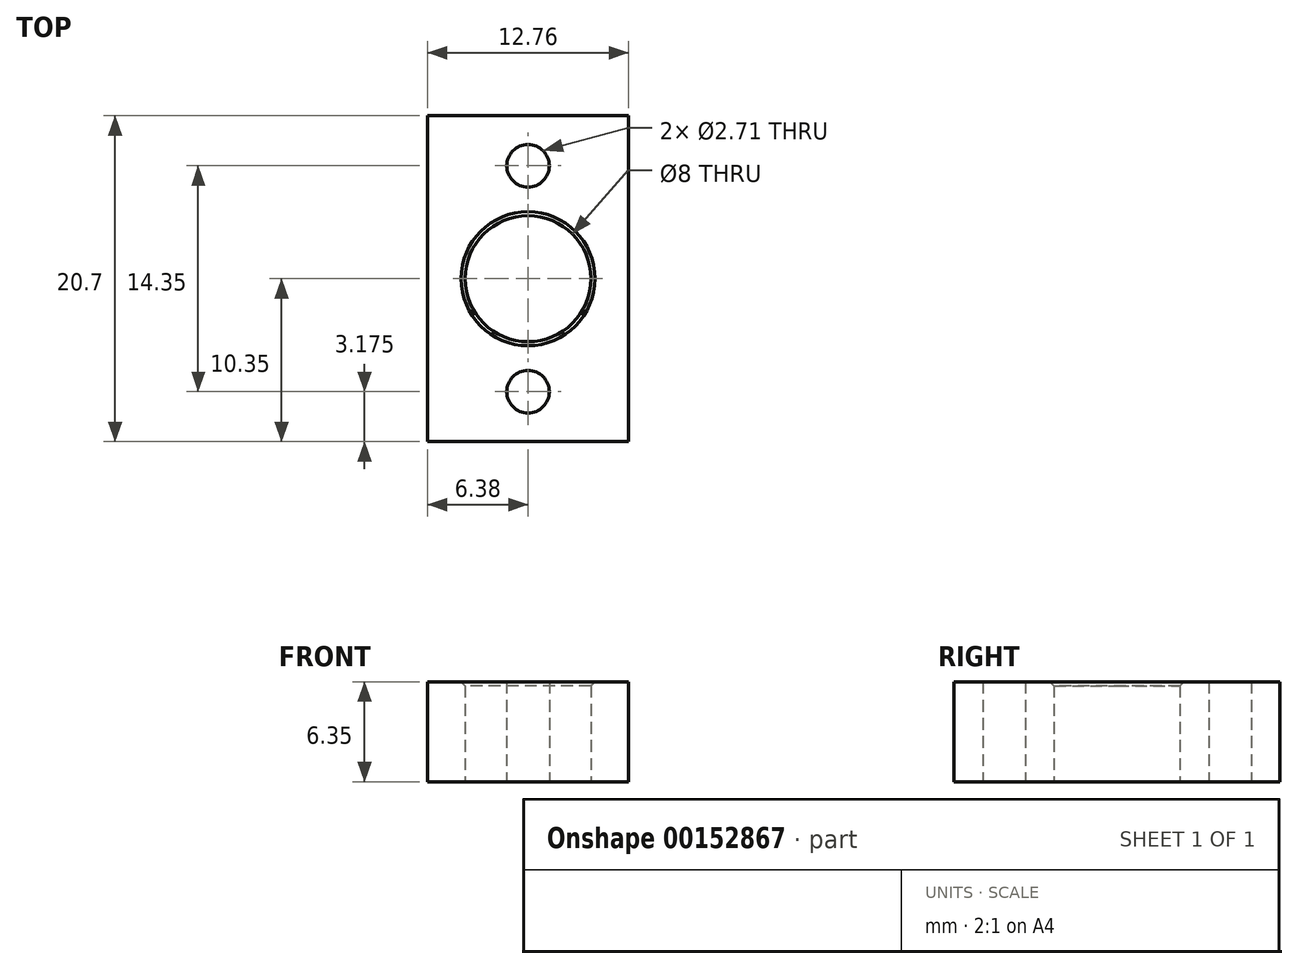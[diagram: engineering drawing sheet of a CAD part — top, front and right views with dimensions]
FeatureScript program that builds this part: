
annotation { "Feature Type Name" : "Feature", "Feature Type Description" : "" }
export const myFeature = defineFeature(function(context is Context, id is Id, definition is map)
    precondition{}
    {
        {
            var Q0;
            Q0=qCreatedBy(makeId("Top.planeOp"),FACE);
            var sketch = newSketch(context, id + "F0", { "sketchPlane" : qUnion([Q0])});
            skLineSegment(sketch, "E0.bottom", {"start": v(6.38, -10.35) * mm, "end": v(-6.38, -10.35) * mm});
            skLineSegment(sketch, "E0.top", {"start": v(6.38, 10.35) * mm, "end": v(-6.38, 10.35) * mm});
            skLineSegment(sketch, "E0.left", {"start": v(6.38, -10.35) * mm, "end": v(6.38, 10.35) * mm});
            skLineSegment(sketch, "E0.right", {"start": v(-6.38, -10.35) * mm, "end": v(-6.38, 10.35) * mm});
            skPoint(sketch, "E0.middle", {"position": v(0, 0) * mm});
            skLineSegment(sketch, "E1", {"start": v(0, -7.18) * mm, "end": v(0, 0) * mm, "construction": true});
            skCircle(sketch, "E2", {"center": v(0, 0) * mm, "radius": 4 * mm});
            skCircle(sketch, "E3", {"center": v(0, -7.18) * mm, "radius": 1.35 * mm});
            skLineSegment(sketch, "E4", {"start": v(0, 0) * mm, "end": v(0, 7.18) * mm, "construction": true});
            skCircle(sketch, "E5", {"center": v(0, 7.18) * mm, "radius": 1.35 * mm});
            skSolve(sketch);
        }
        {
            var Q0;
            Q0=makeQuery(id+"F0.imprint","IMPRINT",FACE,{"disambiguationData":[TD([[makeQuery(id+"F0.imprint","IMPRINT",EDGE,{"derivedFrom":sQuery(id+"F0.wireOp",EDGE,"E0.bottom")}),-1.0]])]});
            extrude(context, id + "F1", {"entities" : qUnion([Q0]), "depth" : 6.35 * mm});
        }
        {
            var Q0;
            Q0=makeQuery(id+"F1.opExtrude","CAP_EDGE",EDGE,{"disambiguationData":[OSD([sQuery(id+"F0.wireOp",EDGE,"E2")])],"isStart":false});
            var Q1;
            Q1=makeQuery(id+"F1.opExtrude","CAP_EDGE",EDGE,{"disambiguationData":[OSD([sQuery(id+"F0.wireOp",EDGE,"YG7tZk8M-4zix-anql-Of3m-cUGt6ix2RjML")])],"isStart":false});
            chamfer(context, id + "F2", {"entities" : qUnion([Q0, Q1]), "width" : 0.25 * mm, "tangentPropagation" : true});
        }
    });
